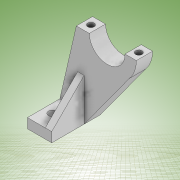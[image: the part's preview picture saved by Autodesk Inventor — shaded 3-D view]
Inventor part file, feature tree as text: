
AUTODESK INVENTOR PART (.ipt)
format: ipt  version: 2022 (Build 260153000, 153)  size: 172,544 bytes
history: native  units: mm
features: sketch x6, extrude x5, other x2
ambient origin geometry x8: Origin, YZ Plane, XZ Plane, XY Plane, X Axis, Y Axis, Z Axis, Center Point
bodies: Body1 (feature_tree)
feature tree (13):
  other  "Sólido1"
  extrude  "Extrusión1"  Depth=50.0mm
  extrude  "Extrusión2"  Depth=6.0mm
  other  "Nervio1"
  extrude  "Extrusión3"  Depth=37.0mm
  extrude  "Extrusión4"  Depth=15.0mm
  extrude  "Extrusión5"  Depth=20.0mm TaperAngle=0.0deg
  sketch  "Boceto1"  dims[d3=50.0mm d4=22.0mm]
  sketch  "Boceto2"  dims[d5=6.0mm d6=21.991149mm]
  sketch  "Boceto3"  dims[d10=13.439035mm d12=37.0mm]
  sketch  "Boceto4"  dims[d13=8.0mm d15=15.0mm]
  sketch  "Boceto5"  dims[d16=10.0mm d17=0.0mm d18=20.0mm d19=0.0mm]
  sketch  "Boceto6"  dims[d20=45.0deg d21=1.0mm d22=4.0mm d23=0.0mm d24=0.0mm d25=1.0mm d26=1.0mm d27=5.0mm d28=10.0mm d29=5.5mm d30=0.0mm d31=0.0mm d32=4.0mm d33=4.0mm d34=0.0mm d35=4.0mm d36=4.0mm d37=0.0mm]
